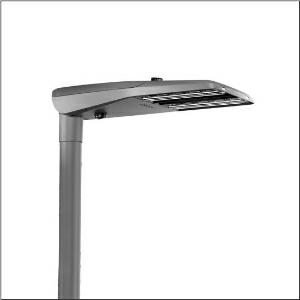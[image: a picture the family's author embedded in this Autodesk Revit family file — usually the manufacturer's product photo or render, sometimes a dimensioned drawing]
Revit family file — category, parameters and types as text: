
# Revit family: streetlight_sl_11_iq_midi___pc-l_5xc3e21y08me_ec69
name_source: partatom
category: Lighting Fixtures
units: mm (PartAtom-declared; Revit-internal decimal feet)

## family parameters
Cut with Voids When Loaded = No
Host = Face
Light Source = No
Part Type = Normal
Room Calculation Point = No
Round Connector Dimension = Use Diameter
Shared = No

## types (1)
- --- (1 x LED, 12730 lm, 122.8 W, 2200K)
    Apparent Load = 123 VA
    CIE Flux Codes = 37 73 96 100 100
    Color Rendering = 70
    Color Temperature = 2200K
    Default Elevation = 1800 mm
    Description = Streetlight SL 11 iQ midi, mast luminaire, primary light control with 3 zone facetted reflector, of plastic, silver coated, highly specular, primary optical cover: cover, of PMMA, transparent, light distribution: PC-L, light emission: direct distribution, primary light characteristic: asymmetric, left, installation type: post-top, side-entry, lamps: LED, High Power LED, rated values: 12.730lm | 122,8W | 103,7lm/W (begin service life); end service life: 12.730lm | 130,2W; at 50% lumin. flux: 6.365lm | 56W | 113,7lm/W, colour temperature: 2200K, colour rendering: CRI > 70, light colour: 722, light setting 1 begin service life: 100% | 12.730lm | 122,8W | 103,7lm/W | 2.200K, light setting 1 end service life: 130,2W, further light settings possible, control: pre-setting: logarithmic dimming characteristic, Street-Remote, Auto-Match, Temp-Guard, Lumen-Switch, Night-Set, Smart-Wire, Light-Fading, Desk-Remote (wireless, voltage-free reading and setting of iQ features in the workshop via application-optimized NFC function/RFID function), optimised constant luminous flux control (CLO 2.0), with cable H07RN-F 3x 1.5mm², mains connection: 230..240V, AC, 50/60Hz, connection cable pre-assembled, cable length: 12,5m, luminaire housing, of diecast aluminium, powder-coated, SITECO metallic grey (DB 702S), please order mast flange separately, inclination adjustable without tools: 0°, 5°, 10°, 15° (post-top) | 0°, -5°, -10°, -15° (side-entry), sealing non-destructively replaceable, multi-level sealing system, length: 780mm, width: 376mm, height: 118mm, mast flange for spigot size: 42mm (side-entry): 5XC10008XM4, 60/48mm (side-entry/post-top): 5XC10108XM2, 76/60mm (side-entry/post-top): 5XC10108XM1, equipment: Power, Smart Interface below and above, protection rating (complete): IP66, insulation class (complete): insulation class II (safety insulation), certification: CE, ENEC, ENEC+, VDE, UKCA, impact resistance: IK10, permissible operating ambient temperature for outdoor applications: -25..+50°C, standard-compliant lighting for roads and squares, Environmental Product Declaration (EPD) tested and certified by an independent institute, packaging unit: 1 piece

Light Distribution: PC-L
    Height = 118 mm
    Lamp = 1 x LED
    Lamp Light Flux = 12730 lm
    Lamp Power = 122.8 W
    Lamp count = 1
    Length = 780 mm
    Luminous efficacy = 104 lm/W
    Manufacturer = Siteco
    ModVariant = No
    Model = 5XC3E21Y08ME
    Number of Poles = 1
    OnlyDefault = Yes
    Power Factor = 1
    Product Name = Streetlight SL 11 iQ midi | PC-L
    Product group = mast luminaire | pylon top
    ProductGroupID = 6100
    Protection Class = Protection class II
    Protection Degree = IP 66
    RLX_Detail_Level = 1
    RLX_Emergency_Light_Flux = 0 lm
    RLX_Emergency_Type = 0
    RLX_Emergency_Type_DB = No
    RlxData = <blob elided: 73701 chars, md5=02063192>
    Socket = socket
    Standby Power = 0 W
    System Light Flux = 12729 lm
    System Power = 123 W
    Type Comments = factory setting: luminous flux: 100 % | dim-lin: 254 | 553 mA
    Type Image = l_1004429.jpg
    URL = http://relux.com
    VarID = @adj_126855
    Voltage = 0 V
    Weight = 0.00 kg
    Width = 376 mm

## geometry (parser evidence)
native form markers: Blend x4, Sweep x11
no freeform markers — native parametric forms only
